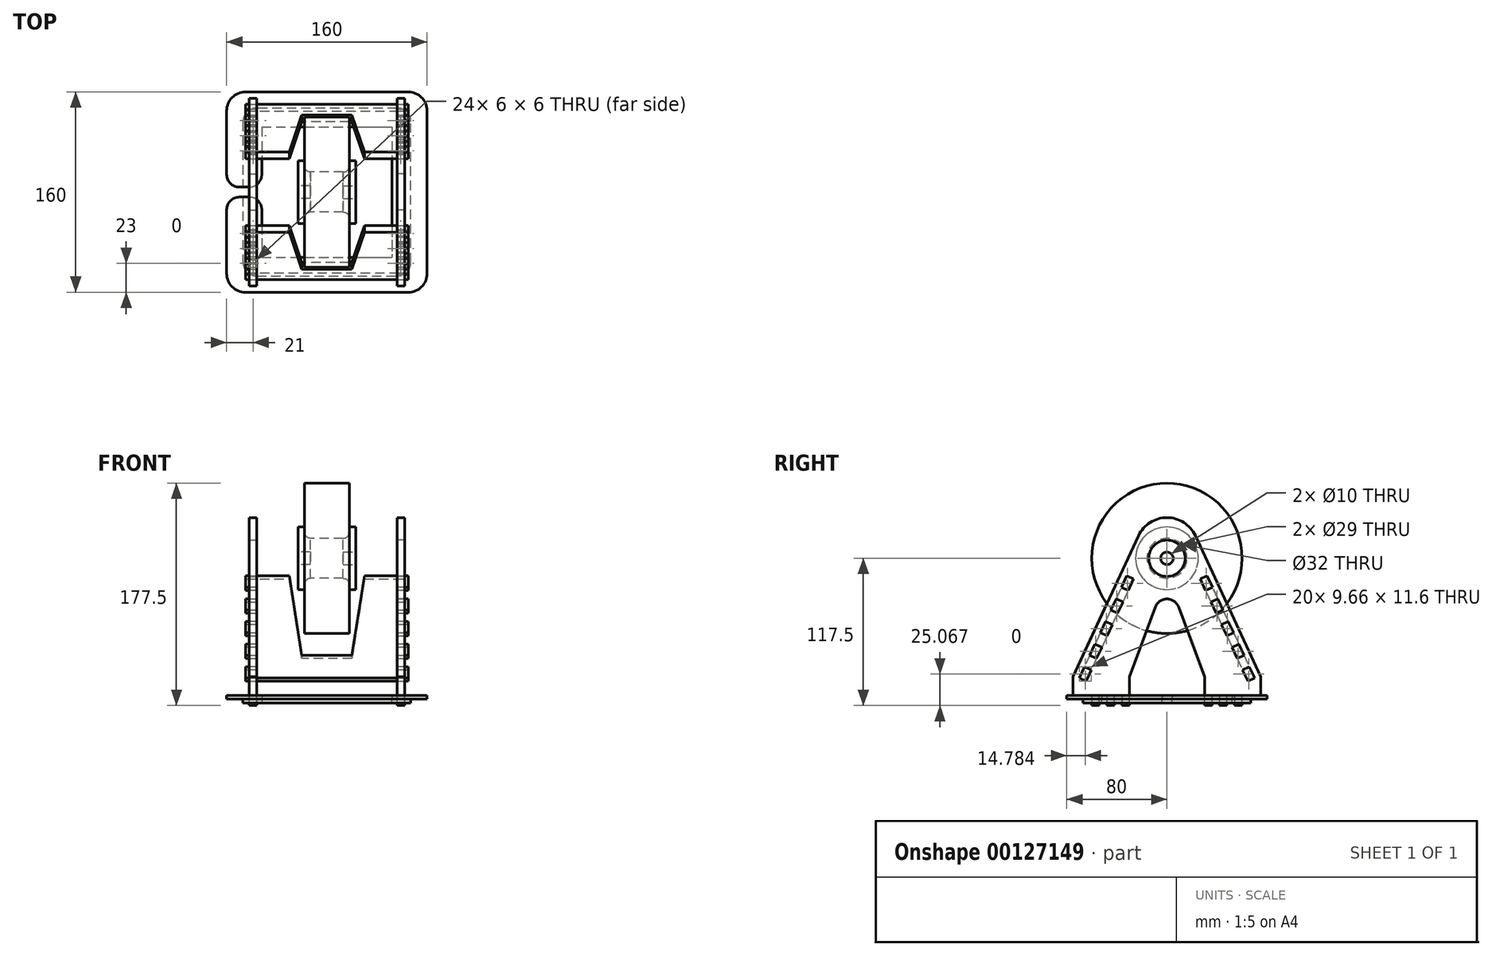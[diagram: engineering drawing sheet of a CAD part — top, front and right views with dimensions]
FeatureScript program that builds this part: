
annotation { "Feature Type Name" : "Feature", "Feature Type Description" : "" }
export const myFeature = defineFeature(function(context is Context, id is Id, definition is map)
    precondition{}
    {
        {
            assignVariable(context, id + "F0", {"name" : "Mat_Halteplatten", "anyValue" : 3});
        }
        {
            assignVariable(context, id + "F1", {"name" : "Mat_Halterung", "anyValue" : 6});
        }
        {
            var Q0;
            Q0=qCreatedBy(makeId("Top.planeOp"),FACE);
            var sketch = newSketch(context, id + "F2", { "sketchPlane" : qUnion([Q0])});
            skLineSegment(sketch, "E0.bottom", {"start": v(67, -67) * mm, "end": v(-67, -67) * mm, "construction": true});
            skLineSegment(sketch, "E0.top", {"start": v(67, 67) * mm, "end": v(-67, 67) * mm, "construction": true});
            skLineSegment(sketch, "E0.left", {"start": v(67, -67) * mm, "end": v(67, 67) * mm, "construction": true});
            skLineSegment(sketch, "E0.right", {"start": v(-67, -67) * mm, "end": v(-67, 67) * mm, "construction": true});
            skPoint(sketch, "E0.middle", {"position": v(0, 0) * mm});
            skLineSegment(sketch, "E1", {"start": v(-67, 56) * mm, "end": v(-67, -56) * mm});
            skLineSegment(sketch, "E2", {"start": v(-56, -67) * mm, "end": v(56, -67) * mm});
            skLineSegment(sketch, "E3", {"start": v(67, -56) * mm, "end": v(67, 56) * mm});
            skLineSegment(sketch, "E4", {"start": v(56, 67) * mm, "end": v(-56, 67) * mm});
            skArc(sketch, "E5", {"start": v(-67, 56) * mm, "mid": v(-63.78, 63.78) * mm, "end": v(-56, 67) * mm});
            skArc(sketch, "E6", {"start": v(67, 56) * mm, "mid": v(63.78, 63.78) * mm, "end": v(56, 67) * mm});
            skArc(sketch, "E7", {"start": v(67, -56) * mm, "mid": v(63.78, -63.78) * mm, "end": v(56, -67) * mm});
            skArc(sketch, "E8", {"start": v(-67, -56) * mm, "mid": v(-63.78, -63.78) * mm, "end": v(-56, -67) * mm});
            skLineSegment(sketch, "E9.bottom", {"start": v(52, -52) * mm, "end": v(-52, -52) * mm});
            skLineSegment(sketch, "E9.top", {"start": v(52, 52) * mm, "end": v(-52, 52) * mm});
            skLineSegment(sketch, "E9.left", {"start": v(52, -52) * mm, "end": v(52, 52) * mm});
            skLineSegment(sketch, "E9.right", {"start": v(-52, -52) * mm, "end": v(-52, 52) * mm});
            skSolve(sketch);
        }
        {
            var Q0;
            Q0 = qSketchRegion(id + "F2", true);
            extrude(context, id + "F3", {"entities" : qUnion([Q0]), "oppositeDirection" : true, "depth" : (getVariable(context, 'Mat_Halteplatten')) * mm});
        }
        {
            var Q0;
            Q0=qCreatedBy(makeId("Top.planeOp"),FACE);
            var sketch = newSketch(context, id + "F4", { "sketchPlane" : qUnion([Q0])});
            skLineSegment(sketch, "E10.bottom", {"start": v(-80, 80) * mm, "end": v(80, 80) * mm});
            skLineSegment(sketch, "E10.top", {"start": v(-80, -80) * mm, "end": v(80, -80) * mm});
            skLineSegment(sketch, "E10.left", {"start": v(-80, 80) * mm, "end": v(-80, -80) * mm});
            skLineSegment(sketch, "E10.right", {"start": v(80, 80) * mm, "end": v(80, -80) * mm});
            skPoint(sketch, "E10.middle", {"position": v(0, 0) * mm});
            skLineSegment(sketch, "E11.bottom", {"start": v(-52, 52) * mm, "end": v(52, 52) * mm});
            skLineSegment(sketch, "E11.top", {"start": v(-52, -52) * mm, "end": v(52, -52) * mm});
            skLineSegment(sketch, "E11.left", {"start": v(-52, 52) * mm, "end": v(-52, -52) * mm});
            skLineSegment(sketch, "E11.right", {"start": v(52, 52) * mm, "end": v(52, -52) * mm});
            skSolve(sketch);
        }
        {
            var Q0;
            Q0 = qSketchRegion(id + "F4", true);
            extrude(context, id + "F5", {"entities" : qUnion([Q0]), "depth" : (getVariable(context, 'Mat_Halteplatten')) * mm});
        }
        {
            var Q0;
            Q0=qCreatedBy(makeId("Right.planeOp"),FACE);
            cPlane(context, id + "F6", {"entities" : qUnion([Q0]), "cplaneType" : CPlaneType.OFFSET, "offset" : 59 * mm, "width" : 150 * mm, "height" : 150 * mm});
        }
        {
            var Q0;
            Q0=qCreatedBy(id+"F6.planeOp",FACE);
            var sketch = newSketch(context, id + "F7", { "sketchPlane" : qUnion([Q0])});
            skArc(sketch, "E12", {"start": v(22.67, 130.54) * mm, "mid": v(0, 145) * mm, "end": v(-22.67, 130.54) * mm});
            skLineSegment(sketch, "E13", {"start": v(-60, 3) * mm, "end": v(-60, -5) * mm});
            skLineSegment(sketch, "E14", {"start": v(-60, -5) * mm, "end": v(-54, -5) * mm});
            skLineSegment(sketch, "E15", {"start": v(-54, -5) * mm, "end": v(-54, 3) * mm});
            skLineSegment(sketch, "E16", {"start": v(-54, 3) * mm, "end": v(-48, 3) * mm});
            skLineSegment(sketch, "E17", {"start": v(-48, 3) * mm, "end": v(-48, -5) * mm});
            skLineSegment(sketch, "E18", {"start": v(-48, -5) * mm, "end": v(-42, -5) * mm});
            skLineSegment(sketch, "E19", {"start": v(-42, -5) * mm, "end": v(-42, 3) * mm});
            skLineSegment(sketch, "E20", {"start": v(-42, 3) * mm, "end": v(-36, 3) * mm});
            skLineSegment(sketch, "E21", {"start": v(-36, 3) * mm, "end": v(-36, -5) * mm});
            skLineSegment(sketch, "E22", {"start": v(-36, -5) * mm, "end": v(-30, -5) * mm});
            skLineSegment(sketch, "E23", {"start": v(-30, -5) * mm, "end": v(-30, 3) * mm});
            skLineSegment(sketch, "E24", {"start": v(30, 3) * mm, "end": v(30, -5) * mm});
            skLineSegment(sketch, "E25", {"start": v(30, -5) * mm, "end": v(36, -5) * mm});
            skLineSegment(sketch, "E26", {"start": v(36, -5) * mm, "end": v(36, 3) * mm});
            skLineSegment(sketch, "E27", {"start": v(36, 3) * mm, "end": v(42, 3) * mm});
            skLineSegment(sketch, "E28", {"start": v(42, 3) * mm, "end": v(42, -5) * mm});
            skLineSegment(sketch, "E29", {"start": v(42, -5) * mm, "end": v(48, -5) * mm});
            skLineSegment(sketch, "E30", {"start": v(48, -5) * mm, "end": v(48, 3) * mm});
            skLineSegment(sketch, "E31", {"start": v(48, 3) * mm, "end": v(54, 3) * mm});
            skLineSegment(sketch, "E32", {"start": v(54, 3) * mm, "end": v(54, -5) * mm});
            skLineSegment(sketch, "E33", {"start": v(54, -5) * mm, "end": v(60, -5) * mm});
            skLineSegment(sketch, "E34", {"start": v(60, -5) * mm, "end": v(60, 3) * mm});
            skLineSegment(sketch, "E35", {"start": v(-30, 3) * mm, "end": v(-30, 18) * mm});
            skLineSegment(sketch, "E36", {"start": v(30, 3) * mm, "end": v(30, 18) * mm});
            skLineSegment(sketch, "E37", {"start": v(-75, 3) * mm, "end": v(-75, 18) * mm});
            skLineSegment(sketch, "E38", {"start": v(75, 3) * mm, "end": v(75, 18) * mm});
            skLineSegment(sketch, "E39", {"start": v(-60, -5) * mm, "end": v(-30, -5) * mm, "construction": true});
            skLineSegment(sketch, "E40", {"start": v(30, -5) * mm, "end": v(60, -5) * mm, "construction": true});
            skLineSegment(sketch, "E41", {"start": v(-75, 18) * mm, "end": v(-22.67, 130.54) * mm});
            skLineSegment(sketch, "E42", {"start": v(22.67, 130.54) * mm, "end": v(75, 18) * mm});
            skArc(sketch, "E43", {"start": v(9.37, 73.48) * mm, "mid": v(0, 80) * mm, "end": v(-9.37, 73.48) * mm});
            skLineSegment(sketch, "E44", {"start": v(-30, 18) * mm, "end": v(-9.37, 73.48) * mm});
            skLineSegment(sketch, "E45", {"start": v(9.37, 73.48) * mm, "end": v(30, 18) * mm});
            skLineSegment(sketch, "E46", {"start": v(0, 80) * mm, "end": v(0, 145) * mm, "construction": true});
            skCircle(sketch, "E47", {"center": v(0, 112.5) * mm, "radius": 14.5 * mm});
            skLineSegment(sketch, "E48", {"start": v(75, 3) * mm, "end": v(60, 3) * mm});
            skLineSegment(sketch, "E49", {"start": v(-60, 3) * mm, "end": v(-75, 3) * mm});
            skSolve(sketch);
        }
        {
            var Q0;
            Q0 = qSketchRegion(id + "F7", true);
            extrude(context, id + "F8", {"entities" : qUnion([Q0]), "endBound" : BoundingType.SYMMETRIC, "depth" : (getVariable(context, 'Mat_Halterung')) * mm});
        }
        {
            var Q0;
            Q0=makeQuery(id+"F8.opExtrude","SWEPT_BODY",BODY,{"disambiguationData":[OSD([sQuery(id+"F7.wireOp",EDGE,"E12"),sQuery(id+"F7.wireOp",EDGE,"E13"),sQuery(id+"F7.wireOp",EDGE,"E14"),sQuery(id+"F7.wireOp",EDGE,"E15"),sQuery(id+"F7.wireOp",EDGE,"E16"),sQuery(id+"F7.wireOp",EDGE,"E17"),sQuery(id+"F7.wireOp",EDGE,"E18"),sQuery(id+"F7.wireOp",EDGE,"E19"),sQuery(id+"F7.wireOp",EDGE,"E20"),sQuery(id+"F7.wireOp",EDGE,"E21"),sQuery(id+"F7.wireOp",EDGE,"E22"),sQuery(id+"F7.wireOp",EDGE,"E23"),sQuery(id+"F7.wireOp",EDGE,"E24"),sQuery(id+"F7.wireOp",EDGE,"E25"),sQuery(id+"F7.wireOp",EDGE,"E26"),sQuery(id+"F7.wireOp",EDGE,"E27"),sQuery(id+"F7.wireOp",EDGE,"E28"),sQuery(id+"F7.wireOp",EDGE,"E29"),sQuery(id+"F7.wireOp",EDGE,"E30"),sQuery(id+"F7.wireOp",EDGE,"E31"),sQuery(id+"F7.wireOp",EDGE,"E32"),sQuery(id+"F7.wireOp",EDGE,"E33"),sQuery(id+"F7.wireOp",EDGE,"E34"),sQuery(id+"F7.wireOp",EDGE,"E35"),sQuery(id+"F7.wireOp",EDGE,"E36"),sQuery(id+"F7.wireOp",EDGE,"E37"),sQuery(id+"F7.wireOp",EDGE,"E38"),sQuery(id+"F7.wireOp",EDGE,"E41"),sQuery(id+"F7.wireOp",EDGE,"E42"),sQuery(id+"F7.wireOp",EDGE,"E43"),sQuery(id+"F7.wireOp",EDGE,"E44"),sQuery(id+"F7.wireOp",EDGE,"E45"),sQuery(id+"F7.wireOp",EDGE,"E47")])]});
            var Q1;
            Q1=qCreatedBy(makeId("Right.planeOp"),FACE);
            mirror(context, id + "F9", {"entities" : qUnion([Q0]), "mirrorPlane" : qUnion([Q1])});
        }
        {
            var Q0;
            Q0=makeQuery(id+"F9.opPattern","COPY",BODY,{"derivedFrom":makeQuery(id+"F8.opExtrude","SWEPT_BODY",BODY,{"disambiguationData":[OSD([sQuery(id+"F7.wireOp",EDGE,"E12"),sQuery(id+"F7.wireOp",EDGE,"E13"),sQuery(id+"F7.wireOp",EDGE,"E14"),sQuery(id+"F7.wireOp",EDGE,"E15"),sQuery(id+"F7.wireOp",EDGE,"E16"),sQuery(id+"F7.wireOp",EDGE,"E17"),sQuery(id+"F7.wireOp",EDGE,"E18"),sQuery(id+"F7.wireOp",EDGE,"E19"),sQuery(id+"F7.wireOp",EDGE,"E20"),sQuery(id+"F7.wireOp",EDGE,"E21"),sQuery(id+"F7.wireOp",EDGE,"E22"),sQuery(id+"F7.wireOp",EDGE,"E23"),sQuery(id+"F7.wireOp",EDGE,"E24"),sQuery(id+"F7.wireOp",EDGE,"E25"),sQuery(id+"F7.wireOp",EDGE,"E26"),sQuery(id+"F7.wireOp",EDGE,"E27"),sQuery(id+"F7.wireOp",EDGE,"E28"),sQuery(id+"F7.wireOp",EDGE,"E29"),sQuery(id+"F7.wireOp",EDGE,"E30"),sQuery(id+"F7.wireOp",EDGE,"E31"),sQuery(id+"F7.wireOp",EDGE,"E32"),sQuery(id+"F7.wireOp",EDGE,"E33"),sQuery(id+"F7.wireOp",EDGE,"E34"),sQuery(id+"F7.wireOp",EDGE,"E35"),sQuery(id+"F7.wireOp",EDGE,"E36"),sQuery(id+"F7.wireOp",EDGE,"E37"),sQuery(id+"F7.wireOp",EDGE,"E38"),sQuery(id+"F7.wireOp",EDGE,"E41"),sQuery(id+"F7.wireOp",EDGE,"E42"),sQuery(id+"F7.wireOp",EDGE,"E43"),sQuery(id+"F7.wireOp",EDGE,"E44"),sQuery(id+"F7.wireOp",EDGE,"E45"),sQuery(id+"F7.wireOp",EDGE,"E47")])]}),"instanceName":"1"});
            var Q1;
            Q1=makeQuery(id+"F8.opExtrude","SWEPT_BODY",BODY,{"disambiguationData":[OSD([sQuery(id+"F7.wireOp",EDGE,"E12"),sQuery(id+"F7.wireOp",EDGE,"E13"),sQuery(id+"F7.wireOp",EDGE,"E14"),sQuery(id+"F7.wireOp",EDGE,"E15"),sQuery(id+"F7.wireOp",EDGE,"E16"),sQuery(id+"F7.wireOp",EDGE,"E17"),sQuery(id+"F7.wireOp",EDGE,"E18"),sQuery(id+"F7.wireOp",EDGE,"E19"),sQuery(id+"F7.wireOp",EDGE,"E20"),sQuery(id+"F7.wireOp",EDGE,"E21"),sQuery(id+"F7.wireOp",EDGE,"E22"),sQuery(id+"F7.wireOp",EDGE,"E23"),sQuery(id+"F7.wireOp",EDGE,"E24"),sQuery(id+"F7.wireOp",EDGE,"E25"),sQuery(id+"F7.wireOp",EDGE,"E26"),sQuery(id+"F7.wireOp",EDGE,"E27"),sQuery(id+"F7.wireOp",EDGE,"E28"),sQuery(id+"F7.wireOp",EDGE,"E29"),sQuery(id+"F7.wireOp",EDGE,"E30"),sQuery(id+"F7.wireOp",EDGE,"E31"),sQuery(id+"F7.wireOp",EDGE,"E32"),sQuery(id+"F7.wireOp",EDGE,"E33"),sQuery(id+"F7.wireOp",EDGE,"E34"),sQuery(id+"F7.wireOp",EDGE,"E35"),sQuery(id+"F7.wireOp",EDGE,"E36"),sQuery(id+"F7.wireOp",EDGE,"E37"),sQuery(id+"F7.wireOp",EDGE,"E38"),sQuery(id+"F7.wireOp",EDGE,"E41"),sQuery(id+"F7.wireOp",EDGE,"E42"),sQuery(id+"F7.wireOp",EDGE,"E43"),sQuery(id+"F7.wireOp",EDGE,"E44"),sQuery(id+"F7.wireOp",EDGE,"E45"),sQuery(id+"F7.wireOp",EDGE,"E47")])]});
            var Q2;
            Q2=makeQuery(id+"F5.opExtrude","SWEPT_BODY",BODY,{"disambiguationData":[OSD([sQuery(id+"F4.wireOp",EDGE,"E10.bottom"),sQuery(id+"F4.wireOp",EDGE,"E10.top"),sQuery(id+"F4.wireOp",EDGE,"E10.left"),sQuery(id+"F4.wireOp",EDGE,"E10.right"),sQuery(id+"F4.wireOp",EDGE,"E11.bottom"),sQuery(id+"F4.wireOp",EDGE,"E11.top"),sQuery(id+"F4.wireOp",EDGE,"E11.left"),sQuery(id+"F4.wireOp",EDGE,"E11.right")])]});
            var Q3;
            Q3=makeQuery(id+"F3.opExtrude","SWEPT_BODY",BODY,{"disambiguationData":[OSD([sQuery(id+"F2.wireOp",EDGE,"E1"),sQuery(id+"F2.wireOp",EDGE,"E2"),sQuery(id+"F2.wireOp",EDGE,"E3"),sQuery(id+"F2.wireOp",EDGE,"E4"),sQuery(id+"F2.wireOp",EDGE,"E5"),sQuery(id+"F2.wireOp",EDGE,"E6"),sQuery(id+"F2.wireOp",EDGE,"E7"),sQuery(id+"F2.wireOp",EDGE,"E8"),sQuery(id+"F2.wireOp",EDGE,"E9.bottom"),sQuery(id+"F2.wireOp",EDGE,"E9.top"),sQuery(id+"F2.wireOp",EDGE,"E9.left"),sQuery(id+"F2.wireOp",EDGE,"E9.right")])]});
            booleanBodies(context, id + "F10", {"operationType" : BooleanOperationType.SUBTRACTION, "tools" : qUnion([Q0, Q1]), "targets" : qUnion([Q2, Q3]), "keepTools" : true});
        }
        {
            var Q0;
            Q0=qCreatedBy(makeId("Right.planeOp"),FACE);
            var sketch = newSketch(context, id + "F11", { "sketchPlane" : qUnion([Q0])});
            skCircle(sketch, "E50", {"center": v(0, 112.5) * mm, "radius": 60 * mm});
            skCircle(sketch, "E51", {"center": v(0, 112.5) * mm, "radius": 16 * mm});
            skSolve(sketch);
        }
        {
            var Q0;
            Q0=makeQuery(id+"F11.imprint","IMPRINT",FACE,{"disambiguationData":[TD([[makeQuery(id+"F11.imprint","IMPRINT",EDGE,{"derivedFrom":sQuery(id+"F11.wireOp",EDGE,"E50")}),1.0]])]});
            extrude(context, id + "F12", {"entities" : qUnion([Q0]), "endBound" : BoundingType.SYMMETRIC, "depth" : 36 * mm});
        }
        {
            var Q0;
            Q0=makeQuery(id+"F9.opPattern","COPY",FACE,{"derivedFrom":makeQuery(id+"F8.opExtrude","SWEPT_FACE",FACE,{"disambiguationData":[OSD([sQuery(id+"F7.wireOp",EDGE,"E41")])]}),"instanceName":"1"});
            var Q1;
            Q1=makeQuery(id+"F8.opExtrude","SWEPT_FACE",FACE,{"disambiguationData":[OSD([sQuery(id+"F7.wireOp",EDGE,"E41")])]});
            cPlane(context, id + "F13", {"entities" : qUnion([Q0, Q1]), "cplaneType" : CPlaneType.MID_PLANE, "offset" : 0 * mm, "width" : 150 * mm, "height" : 150 * mm});
        }
        {
            var Q0;
            Q0=qCreatedBy(id+"F13.planeOp",FACE);
            cPlane(context, id + "F14", {"entities" : qUnion([Q0]), "cplaneType" : CPlaneType.OFFSET, "offset" : 8 * mm, "oppositeDirection" : true, "width" : 150 * mm, "height" : 150 * mm});
        }
        {
            var Q0;
            Q0=qCreatedBy(id+"F14.planeOp",FACE);
            var sketch = newSketch(context, id + "F15", { "sketchPlane" : qUnion([Q0])});
            skLineSegment(sketch, "E52", {"start": v(-65, -14.3) * mm, "end": v(65, -14.3) * mm});
            skLineSegment(sketch, "E53", {"start": v(65, -14.3) * mm, "end": v(65, -4.3) * mm});
            skLineSegment(sketch, "E54", {"start": v(65, -4.3) * mm, "end": v(56, -4.3) * mm});
            skLineSegment(sketch, "E55", {"start": v(56, -4.3) * mm, "end": v(56, 5.7) * mm});
            skLineSegment(sketch, "E56", {"start": v(56, 5.7) * mm, "end": v(65, 5.7) * mm});
            skLineSegment(sketch, "E57", {"start": v(65, 5.7) * mm, "end": v(65, 15.7) * mm});
            skLineSegment(sketch, "E58", {"start": v(65, 15.7) * mm, "end": v(56, 15.7) * mm});
            skLineSegment(sketch, "E59", {"start": v(56, 15.7) * mm, "end": v(56, 25.7) * mm});
            skLineSegment(sketch, "E60", {"start": v(56, 25.7) * mm, "end": v(65, 25.7) * mm});
            skLineSegment(sketch, "E61", {"start": v(65, 25.7) * mm, "end": v(65, 35.7) * mm});
            skLineSegment(sketch, "E62", {"start": v(65, 35.7) * mm, "end": v(56, 35.7) * mm});
            skLineSegment(sketch, "E63", {"start": v(56, 35.7) * mm, "end": v(56, 45.7) * mm});
            skLineSegment(sketch, "E64", {"start": v(56, 45.7) * mm, "end": v(65, 45.7) * mm});
            skLineSegment(sketch, "E65", {"start": v(65, 45.7) * mm, "end": v(65, 55.7) * mm});
            skLineSegment(sketch, "E66", {"start": v(30, 75.7) * mm, "end": v(20, 5.7) * mm});
            skLineSegment(sketch, "E67", {"start": v(20, 5.7) * mm, "end": v(-20, 5.7) * mm});
            skLineSegment(sketch, "E68", {"start": v(-20, 5.7) * mm, "end": v(-30, 75.7) * mm});
            skLineSegment(sketch, "E69", {"start": v(-65, 55.7) * mm, "end": v(-65, 45.7) * mm});
            skLineSegment(sketch, "E70", {"start": v(-65, 45.7) * mm, "end": v(-56, 45.7) * mm});
            skLineSegment(sketch, "E71", {"start": v(-56, 45.7) * mm, "end": v(-56, 35.7) * mm});
            skLineSegment(sketch, "E72", {"start": v(-56, 35.7) * mm, "end": v(-65, 35.7) * mm});
            skLineSegment(sketch, "E73", {"start": v(-65, 35.7) * mm, "end": v(-65, 25.7) * mm});
            skLineSegment(sketch, "E74", {"start": v(-65, 25.7) * mm, "end": v(-56, 25.7) * mm});
            skLineSegment(sketch, "E75", {"start": v(-56, 25.7) * mm, "end": v(-56, 15.7) * mm});
            skLineSegment(sketch, "E76", {"start": v(-56, 15.7) * mm, "end": v(-65, 15.7) * mm});
            skLineSegment(sketch, "E77", {"start": v(-65, 15.7) * mm, "end": v(-65, 5.7) * mm});
            skLineSegment(sketch, "E78", {"start": v(-65, 5.7) * mm, "end": v(-56, 5.7) * mm});
            skLineSegment(sketch, "E79", {"start": v(-56, 5.7) * mm, "end": v(-56, -4.3) * mm});
            skLineSegment(sketch, "E80", {"start": v(-56, -4.3) * mm, "end": v(-65, -4.3) * mm});
            skLineSegment(sketch, "E81", {"start": v(-65, -4.3) * mm, "end": v(-65, -14.3) * mm});
            skLineSegment(sketch, "E82", {"start": v(-65, 55.7) * mm, "end": v(-56, 55.7) * mm});
            skLineSegment(sketch, "E83", {"start": v(-56, 55.7) * mm, "end": v(-56, 65.7) * mm});
            skLineSegment(sketch, "E84", {"start": v(-56, 65.7) * mm, "end": v(-65, 65.7) * mm});
            skLineSegment(sketch, "E85", {"start": v(-65, 65.7) * mm, "end": v(-65, 75.7) * mm});
            skLineSegment(sketch, "E86", {"start": v(-65, 75.7) * mm, "end": v(-30, 75.7) * mm});
            skLineSegment(sketch, "E87", {"start": v(30, 75.7) * mm, "end": v(65, 75.7) * mm});
            skLineSegment(sketch, "E88", {"start": v(65, 75.7) * mm, "end": v(65, 65.7) * mm});
            skLineSegment(sketch, "E89", {"start": v(65, 65.7) * mm, "end": v(56, 65.7) * mm});
            skLineSegment(sketch, "E90", {"start": v(56, 65.7) * mm, "end": v(56, 55.7) * mm});
            skLineSegment(sketch, "E91", {"start": v(56, 55.7) * mm, "end": v(65, 55.7) * mm});
            skSolve(sketch);
        }
        {
            var Q0;
            Q0 = qSketchRegion(id + "F15", true);
            extrude(context, id + "F16", {"entities" : qUnion([Q0]), "endBound" : BoundingType.SYMMETRIC, "depth" : (getVariable(context, 'Mat_Halterung')) * mm});
        }
        {
            var Q0;
            Q0=makeQuery(id+"F16.opExtrude","SWEPT_BODY",BODY,{"disambiguationData":[OSD([sQuery(id+"F15.wireOp",EDGE,"E52"),sQuery(id+"F15.wireOp",EDGE,"E53"),sQuery(id+"F15.wireOp",EDGE,"E54"),sQuery(id+"F15.wireOp",EDGE,"E55"),sQuery(id+"F15.wireOp",EDGE,"E56"),sQuery(id+"F15.wireOp",EDGE,"E57"),sQuery(id+"F15.wireOp",EDGE,"E58"),sQuery(id+"F15.wireOp",EDGE,"E59"),sQuery(id+"F15.wireOp",EDGE,"E60"),sQuery(id+"F15.wireOp",EDGE,"E61"),sQuery(id+"F15.wireOp",EDGE,"E62"),sQuery(id+"F15.wireOp",EDGE,"E63"),sQuery(id+"F15.wireOp",EDGE,"E64"),sQuery(id+"F15.wireOp",EDGE,"E65"),sQuery(id+"F15.wireOp",EDGE,"E66"),sQuery(id+"F15.wireOp",EDGE,"E67"),sQuery(id+"F15.wireOp",EDGE,"E68"),sQuery(id+"F15.wireOp",EDGE,"E69"),sQuery(id+"F15.wireOp",EDGE,"E70"),sQuery(id+"F15.wireOp",EDGE,"E71"),sQuery(id+"F15.wireOp",EDGE,"E72"),sQuery(id+"F15.wireOp",EDGE,"E73"),sQuery(id+"F15.wireOp",EDGE,"E74"),sQuery(id+"F15.wireOp",EDGE,"E75"),sQuery(id+"F15.wireOp",EDGE,"E76"),sQuery(id+"F15.wireOp",EDGE,"E77"),sQuery(id+"F15.wireOp",EDGE,"E78"),sQuery(id+"F15.wireOp",EDGE,"E79"),sQuery(id+"F15.wireOp",EDGE,"E80"),sQuery(id+"F15.wireOp",EDGE,"E81"),sQuery(id+"F15.wireOp",EDGE,"E82"),sQuery(id+"F15.wireOp",EDGE,"E83"),sQuery(id+"F15.wireOp",EDGE,"E84"),sQuery(id+"F15.wireOp",EDGE,"E85"),sQuery(id+"F15.wireOp",EDGE,"E86"),sQuery(id+"F15.wireOp",EDGE,"E87"),sQuery(id+"F15.wireOp",EDGE,"E88"),sQuery(id+"F15.wireOp",EDGE,"E89"),sQuery(id+"F15.wireOp",EDGE,"E90"),sQuery(id+"F15.wireOp",EDGE,"E91")])]});
            var Q1;
            Q1=qCreatedBy(makeId("Front.planeOp"),FACE);
            mirror(context, id + "F17", {"entities" : qUnion([Q0]), "mirrorPlane" : qUnion([Q1])});
        }
        {
            var Q0;
            Q0=makeQuery(id+"F17.opPattern","COPY",BODY,{"derivedFrom":makeQuery(id+"F16.opExtrude","SWEPT_BODY",BODY,{"disambiguationData":[OSD([sQuery(id+"F15.wireOp",EDGE,"E52"),sQuery(id+"F15.wireOp",EDGE,"E53"),sQuery(id+"F15.wireOp",EDGE,"E54"),sQuery(id+"F15.wireOp",EDGE,"E55"),sQuery(id+"F15.wireOp",EDGE,"E56"),sQuery(id+"F15.wireOp",EDGE,"E57"),sQuery(id+"F15.wireOp",EDGE,"E58"),sQuery(id+"F15.wireOp",EDGE,"E59"),sQuery(id+"F15.wireOp",EDGE,"E60"),sQuery(id+"F15.wireOp",EDGE,"E61"),sQuery(id+"F15.wireOp",EDGE,"E62"),sQuery(id+"F15.wireOp",EDGE,"E63"),sQuery(id+"F15.wireOp",EDGE,"E64"),sQuery(id+"F15.wireOp",EDGE,"E65"),sQuery(id+"F15.wireOp",EDGE,"E66"),sQuery(id+"F15.wireOp",EDGE,"E67"),sQuery(id+"F15.wireOp",EDGE,"E68"),sQuery(id+"F15.wireOp",EDGE,"E69"),sQuery(id+"F15.wireOp",EDGE,"E70"),sQuery(id+"F15.wireOp",EDGE,"E71"),sQuery(id+"F15.wireOp",EDGE,"E72"),sQuery(id+"F15.wireOp",EDGE,"E73"),sQuery(id+"F15.wireOp",EDGE,"E74"),sQuery(id+"F15.wireOp",EDGE,"E75"),sQuery(id+"F15.wireOp",EDGE,"E76"),sQuery(id+"F15.wireOp",EDGE,"E77"),sQuery(id+"F15.wireOp",EDGE,"E78"),sQuery(id+"F15.wireOp",EDGE,"E79"),sQuery(id+"F15.wireOp",EDGE,"E80"),sQuery(id+"F15.wireOp",EDGE,"E81"),sQuery(id+"F15.wireOp",EDGE,"E82"),sQuery(id+"F15.wireOp",EDGE,"E83"),sQuery(id+"F15.wireOp",EDGE,"E84"),sQuery(id+"F15.wireOp",EDGE,"E85"),sQuery(id+"F15.wireOp",EDGE,"E86"),sQuery(id+"F15.wireOp",EDGE,"E87"),sQuery(id+"F15.wireOp",EDGE,"E88"),sQuery(id+"F15.wireOp",EDGE,"E89"),sQuery(id+"F15.wireOp",EDGE,"E90"),sQuery(id+"F15.wireOp",EDGE,"E91")])]}),"instanceName":"1"});
            var Q1;
            Q1=makeQuery(id+"F16.opExtrude","SWEPT_BODY",BODY,{"disambiguationData":[OSD([sQuery(id+"F15.wireOp",EDGE,"E52"),sQuery(id+"F15.wireOp",EDGE,"E53"),sQuery(id+"F15.wireOp",EDGE,"E54"),sQuery(id+"F15.wireOp",EDGE,"E55"),sQuery(id+"F15.wireOp",EDGE,"E56"),sQuery(id+"F15.wireOp",EDGE,"E57"),sQuery(id+"F15.wireOp",EDGE,"E58"),sQuery(id+"F15.wireOp",EDGE,"E59"),sQuery(id+"F15.wireOp",EDGE,"E60"),sQuery(id+"F15.wireOp",EDGE,"E61"),sQuery(id+"F15.wireOp",EDGE,"E62"),sQuery(id+"F15.wireOp",EDGE,"E63"),sQuery(id+"F15.wireOp",EDGE,"E64"),sQuery(id+"F15.wireOp",EDGE,"E65"),sQuery(id+"F15.wireOp",EDGE,"E66"),sQuery(id+"F15.wireOp",EDGE,"E67"),sQuery(id+"F15.wireOp",EDGE,"E68"),sQuery(id+"F15.wireOp",EDGE,"E69"),sQuery(id+"F15.wireOp",EDGE,"E70"),sQuery(id+"F15.wireOp",EDGE,"E71"),sQuery(id+"F15.wireOp",EDGE,"E72"),sQuery(id+"F15.wireOp",EDGE,"E73"),sQuery(id+"F15.wireOp",EDGE,"E74"),sQuery(id+"F15.wireOp",EDGE,"E75"),sQuery(id+"F15.wireOp",EDGE,"E76"),sQuery(id+"F15.wireOp",EDGE,"E77"),sQuery(id+"F15.wireOp",EDGE,"E78"),sQuery(id+"F15.wireOp",EDGE,"E79"),sQuery(id+"F15.wireOp",EDGE,"E80"),sQuery(id+"F15.wireOp",EDGE,"E81"),sQuery(id+"F15.wireOp",EDGE,"E82"),sQuery(id+"F15.wireOp",EDGE,"E83"),sQuery(id+"F15.wireOp",EDGE,"E84"),sQuery(id+"F15.wireOp",EDGE,"E85"),sQuery(id+"F15.wireOp",EDGE,"E86"),sQuery(id+"F15.wireOp",EDGE,"E87"),sQuery(id+"F15.wireOp",EDGE,"E88"),sQuery(id+"F15.wireOp",EDGE,"E89"),sQuery(id+"F15.wireOp",EDGE,"E90"),sQuery(id+"F15.wireOp",EDGE,"E91")])]});
            var Q2;
            Q2=makeQuery(id+"F9.opPattern","COPY",BODY,{"derivedFrom":makeQuery(id+"F8.opExtrude","SWEPT_BODY",BODY,{"disambiguationData":[OSD([sQuery(id+"F7.wireOp",EDGE,"E12"),sQuery(id+"F7.wireOp",EDGE,"E13"),sQuery(id+"F7.wireOp",EDGE,"E14"),sQuery(id+"F7.wireOp",EDGE,"E15"),sQuery(id+"F7.wireOp",EDGE,"E16"),sQuery(id+"F7.wireOp",EDGE,"E17"),sQuery(id+"F7.wireOp",EDGE,"E18"),sQuery(id+"F7.wireOp",EDGE,"E19"),sQuery(id+"F7.wireOp",EDGE,"E20"),sQuery(id+"F7.wireOp",EDGE,"E21"),sQuery(id+"F7.wireOp",EDGE,"E22"),sQuery(id+"F7.wireOp",EDGE,"E23"),sQuery(id+"F7.wireOp",EDGE,"E24"),sQuery(id+"F7.wireOp",EDGE,"E25"),sQuery(id+"F7.wireOp",EDGE,"E26"),sQuery(id+"F7.wireOp",EDGE,"E27"),sQuery(id+"F7.wireOp",EDGE,"E28"),sQuery(id+"F7.wireOp",EDGE,"E29"),sQuery(id+"F7.wireOp",EDGE,"E30"),sQuery(id+"F7.wireOp",EDGE,"E31"),sQuery(id+"F7.wireOp",EDGE,"E32"),sQuery(id+"F7.wireOp",EDGE,"E33"),sQuery(id+"F7.wireOp",EDGE,"E34"),sQuery(id+"F7.wireOp",EDGE,"E35"),sQuery(id+"F7.wireOp",EDGE,"E36"),sQuery(id+"F7.wireOp",EDGE,"E37"),sQuery(id+"F7.wireOp",EDGE,"E38"),sQuery(id+"F7.wireOp",EDGE,"E41"),sQuery(id+"F7.wireOp",EDGE,"E42"),sQuery(id+"F7.wireOp",EDGE,"E43"),sQuery(id+"F7.wireOp",EDGE,"E44"),sQuery(id+"F7.wireOp",EDGE,"E45"),sQuery(id+"F7.wireOp",EDGE,"E47"),sQuery(id+"F7.wireOp",EDGE,"E48"),sQuery(id+"F7.wireOp",EDGE,"E49")])]}),"instanceName":"1"});
            var Q3;
            Q3=makeQuery(id+"F8.opExtrude","SWEPT_BODY",BODY,{"disambiguationData":[OSD([sQuery(id+"F7.wireOp",EDGE,"E12"),sQuery(id+"F7.wireOp",EDGE,"E13"),sQuery(id+"F7.wireOp",EDGE,"E14"),sQuery(id+"F7.wireOp",EDGE,"E15"),sQuery(id+"F7.wireOp",EDGE,"E16"),sQuery(id+"F7.wireOp",EDGE,"E17"),sQuery(id+"F7.wireOp",EDGE,"E18"),sQuery(id+"F7.wireOp",EDGE,"E19"),sQuery(id+"F7.wireOp",EDGE,"E20"),sQuery(id+"F7.wireOp",EDGE,"E21"),sQuery(id+"F7.wireOp",EDGE,"E22"),sQuery(id+"F7.wireOp",EDGE,"E23"),sQuery(id+"F7.wireOp",EDGE,"E24"),sQuery(id+"F7.wireOp",EDGE,"E25"),sQuery(id+"F7.wireOp",EDGE,"E26"),sQuery(id+"F7.wireOp",EDGE,"E27"),sQuery(id+"F7.wireOp",EDGE,"E28"),sQuery(id+"F7.wireOp",EDGE,"E29"),sQuery(id+"F7.wireOp",EDGE,"E30"),sQuery(id+"F7.wireOp",EDGE,"E31"),sQuery(id+"F7.wireOp",EDGE,"E32"),sQuery(id+"F7.wireOp",EDGE,"E33"),sQuery(id+"F7.wireOp",EDGE,"E34"),sQuery(id+"F7.wireOp",EDGE,"E35"),sQuery(id+"F7.wireOp",EDGE,"E36"),sQuery(id+"F7.wireOp",EDGE,"E37"),sQuery(id+"F7.wireOp",EDGE,"E38"),sQuery(id+"F7.wireOp",EDGE,"E41"),sQuery(id+"F7.wireOp",EDGE,"E42"),sQuery(id+"F7.wireOp",EDGE,"E43"),sQuery(id+"F7.wireOp",EDGE,"E44"),sQuery(id+"F7.wireOp",EDGE,"E45"),sQuery(id+"F7.wireOp",EDGE,"E47"),sQuery(id+"F7.wireOp",EDGE,"E48"),sQuery(id+"F7.wireOp",EDGE,"E49")])]});
            booleanBodies(context, id + "F18", {"operationType" : BooleanOperationType.SUBTRACTION, "tools" : qUnion([Q0, Q1]), "targets" : qUnion([Q2, Q3]), "keepTools" : true});
        }
        {
            var Q0;
            Q0=qCreatedBy(makeId("Front.planeOp"),FACE);
            var sketch = newSketch(context, id + "F19", { "sketchPlane" : qUnion([Q0])});
            skLineSegment(sketch, "E92.bottom", {"start": v(-45, -10) * mm, "end": v(-85, -10) * mm});
            skLineSegment(sketch, "E92.top", {"start": v(-45, 10) * mm, "end": v(-85, 10) * mm});
            skLineSegment(sketch, "E92.left", {"start": v(-45, -10) * mm, "end": v(-45, 10) * mm});
            skLineSegment(sketch, "E92.right", {"start": v(-85, -10) * mm, "end": v(-85, 10) * mm});
            skPoint(sketch, "E92.middle", {"position": v(-65, 0) * mm});
            skSolve(sketch);
        }
        {
            var Q0;
            Q0 = qSketchRegion(id + "F19", true);
            extrude(context, id + "F20", {"entities" : qUnion([Q0]), "operationType" : NewBodyOperationType.REMOVE, "endBound" : BoundingType.SYMMETRIC, "depth" : 8 * mm});
        }
        {
            var Q0;
            Q0=makeQuery(id+"F20.boolean.opBoolean","INTERSECT",EDGE,{"derivedFrom":[makeQuery(id+"F5.opExtrude","SWEPT_FACE",FACE,{"disambiguationData":[OSD([sQuery(id+"F4.wireOp",EDGE,"E10.left")])]}),makeQuery(id+"F20.opExtrude","CAP_FACE",FACE,{"disambiguationData":[OSD([sQuery(id+"F19.wireOp",EDGE,"E92.bottom"),sQuery(id+"F19.wireOp",EDGE,"E92.top"),sQuery(id+"F19.wireOp",EDGE,"E92.left"),sQuery(id+"F19.wireOp",EDGE,"E92.right")])],"isStart":true})]});
            var Q1;
            Q1=makeQuery(id+"F20.boolean.opBoolean","INTERSECT",EDGE,{"derivedFrom":[makeQuery(id+"F5.opExtrude","SWEPT_FACE",FACE,{"disambiguationData":[OSD([sQuery(id+"F4.wireOp",EDGE,"E10.left")])]}),makeQuery(id+"F20.opExtrude","CAP_FACE",FACE,{"disambiguationData":[OSD([sQuery(id+"F19.wireOp",EDGE,"E92.bottom"),sQuery(id+"F19.wireOp",EDGE,"E92.top"),sQuery(id+"F19.wireOp",EDGE,"E92.left"),sQuery(id+"F19.wireOp",EDGE,"E92.right")])],"isStart":false})]});
            var Q2;
            Q2=makeQuery(id+"F20.boolean.opBoolean","INTERSECT",EDGE,{"derivedFrom":[makeQuery(id+"F5.opExtrude","SWEPT_FACE",FACE,{"disambiguationData":[OSD([sQuery(id+"F4.wireOp",EDGE,"E11.left")])]}),makeQuery(id+"F20.opExtrude","CAP_FACE",FACE,{"disambiguationData":[OSD([sQuery(id+"F19.wireOp",EDGE,"E92.bottom"),sQuery(id+"F19.wireOp",EDGE,"E92.top"),sQuery(id+"F19.wireOp",EDGE,"E92.left"),sQuery(id+"F19.wireOp",EDGE,"E92.right")])],"isStart":true})]});
            var Q3;
            Q3=makeQuery(id+"F20.boolean.opBoolean","INTERSECT",EDGE,{"derivedFrom":[makeQuery(id+"F3.opExtrude","SWEPT_FACE",FACE,{"disambiguationData":[OSD([sQuery(id+"F2.wireOp",EDGE,"E9.right")])]}),makeQuery(id+"F20.opExtrude","CAP_FACE",FACE,{"disambiguationData":[OSD([sQuery(id+"F19.wireOp",EDGE,"E92.bottom"),sQuery(id+"F19.wireOp",EDGE,"E92.top"),sQuery(id+"F19.wireOp",EDGE,"E92.left"),sQuery(id+"F19.wireOp",EDGE,"E92.right")])],"isStart":true})]});
            var Q4;
            Q4=makeQuery(id+"F20.boolean.opBoolean","INTERSECT",EDGE,{"derivedFrom":[makeQuery(id+"F3.opExtrude","SWEPT_FACE",FACE,{"disambiguationData":[OSD([sQuery(id+"F2.wireOp",EDGE,"E9.right")])]}),makeQuery(id+"F20.opExtrude","CAP_FACE",FACE,{"disambiguationData":[OSD([sQuery(id+"F19.wireOp",EDGE,"E92.bottom"),sQuery(id+"F19.wireOp",EDGE,"E92.top"),sQuery(id+"F19.wireOp",EDGE,"E92.left"),sQuery(id+"F19.wireOp",EDGE,"E92.right")])],"isStart":false})]});
            var Q5;
            Q5=makeQuery(id+"F20.boolean.opBoolean","INTERSECT",EDGE,{"derivedFrom":[makeQuery(id+"F5.opExtrude","SWEPT_FACE",FACE,{"disambiguationData":[OSD([sQuery(id+"F4.wireOp",EDGE,"E11.left")])]}),makeQuery(id+"F20.opExtrude","CAP_FACE",FACE,{"disambiguationData":[OSD([sQuery(id+"F19.wireOp",EDGE,"E92.bottom"),sQuery(id+"F19.wireOp",EDGE,"E92.top"),sQuery(id+"F19.wireOp",EDGE,"E92.left"),sQuery(id+"F19.wireOp",EDGE,"E92.right")])],"isStart":false})]});
            fillet(context, id + "F21", {"entities" : qUnion([Q0, Q1, Q2, Q3, Q4, Q5]), "radius" : 10 * mm, "tangentPropagation" : true, "allowEdgeOverflow" : false});
        }
        {
            var Q0;
            Q0=makeQuery(id+"F5.opExtrude","SWEPT_EDGE",EDGE,{"disambiguationData":[OSD([sQuery(id+"F4.wireOp",EDGE,"E10.top"),sQuery(id+"F4.wireOp",EDGE,"E10.left")])]});
            var Q1;
            Q1=makeQuery(id+"F5.opExtrude","SWEPT_EDGE",EDGE,{"disambiguationData":[OSD([sQuery(id+"F4.wireOp",EDGE,"E10.top"),sQuery(id+"F4.wireOp",EDGE,"E10.right")])]});
            var Q2;
            Q2=makeQuery(id+"F5.opExtrude","SWEPT_EDGE",EDGE,{"disambiguationData":[OSD([sQuery(id+"F4.wireOp",EDGE,"E10.bottom"),sQuery(id+"F4.wireOp",EDGE,"E10.right")])]});
            var Q3;
            Q3=makeQuery(id+"F5.opExtrude","SWEPT_EDGE",EDGE,{"disambiguationData":[OSD([sQuery(id+"F4.wireOp",EDGE,"E10.bottom"),sQuery(id+"F4.wireOp",EDGE,"E10.left")])]});
            fillet(context, id + "F22", {"entities" : qUnion([Q0, Q1, Q2, Q3]), "radius" : 15 * mm, "tangentPropagation" : true, "allowEdgeOverflow" : false});
        }
        {
            var Q0;
            Q0=makeQuery(id+"F12.opExtrude","CAP_EDGE",EDGE,{"disambiguationData":[OSD([sQuery(id+"F11.wireOp",EDGE,"E51")])],"isStart":false});
            var Q1;
            Q1=makeQuery(id+"F12.opExtrude","CAP_EDGE",EDGE,{"disambiguationData":[OSD([sQuery(id+"F11.wireOp",EDGE,"E51")])],"isStart":true});
            fillet(context, id + "F23", {"entities" : qUnion([Q0, Q1]), "radius" : 5 * mm, "tangentPropagation" : true, "allowEdgeOverflow" : false});
        }
        {
            var Q0;
            Q0=makeQuery(id+"F12.opExtrude","CAP_FACE",FACE,{"disambiguationData":[OSD([sQuery(id+"F11.wireOp",EDGE,"E50"),sQuery(id+"F11.wireOp",EDGE,"E51")])],"isStart":true});
            var sketch = newSketch(context, id + "F24", { "sketchPlane" : qUnion([Q0])});
            skCircle(sketch, "E93", {"center": v(0, 112.5) * mm, "radius": 25 * mm});
            skCircle(sketch, "E94", {"center": v(0, 112.5) * mm, "radius": 5 * mm});
            skSolve(sketch);
        }
        {
            var Q0;
            Q0 = qSketchRegion(id + "F24", true);
            extrude(context, id + "F25", {"entities" : qUnion([Q0]), "endBound" : BoundingType.SYMMETRIC, "oppositeDirection" : true, "depth" : 10 * mm});
        }
        {
            var Q0;
            Q0=makeQuery(id+"F12.opExtrude","SWEPT_BODY",BODY,{"disambiguationData":[OSD([sQuery(id+"F11.wireOp",EDGE,"E50"),sQuery(id+"F11.wireOp",EDGE,"E51")])]});
            var Q1;
            Q1=makeQuery(id+"F25.opExtrude","SWEPT_BODY",BODY,{"disambiguationData":[OSD([sQuery(id+"F24.wireOp",EDGE,"E93"),sQuery(id+"F24.wireOp",EDGE,"E94")])]});
            booleanBodies(context, id + "F26", {"operationType" : BooleanOperationType.SUBTRACTION, "tools" : qUnion([Q0]), "targets" : qUnion([Q1]), "keepTools" : true});
        }
        {
            var Q0;
            Q0=makeQuery(id+"F25.opExtrude","SWEPT_BODY",BODY,{"disambiguationData":[OSD([sQuery(id+"F24.wireOp",EDGE,"E93"),sQuery(id+"F24.wireOp",EDGE,"E94")])]});
            var Q1;
            Q1=qCreatedBy(makeId("Right.planeOp"),FACE);
            mirror(context, id + "F27", {"entities" : qUnion([Q0]), "mirrorPlane" : qUnion([Q1])});
        }
    });
